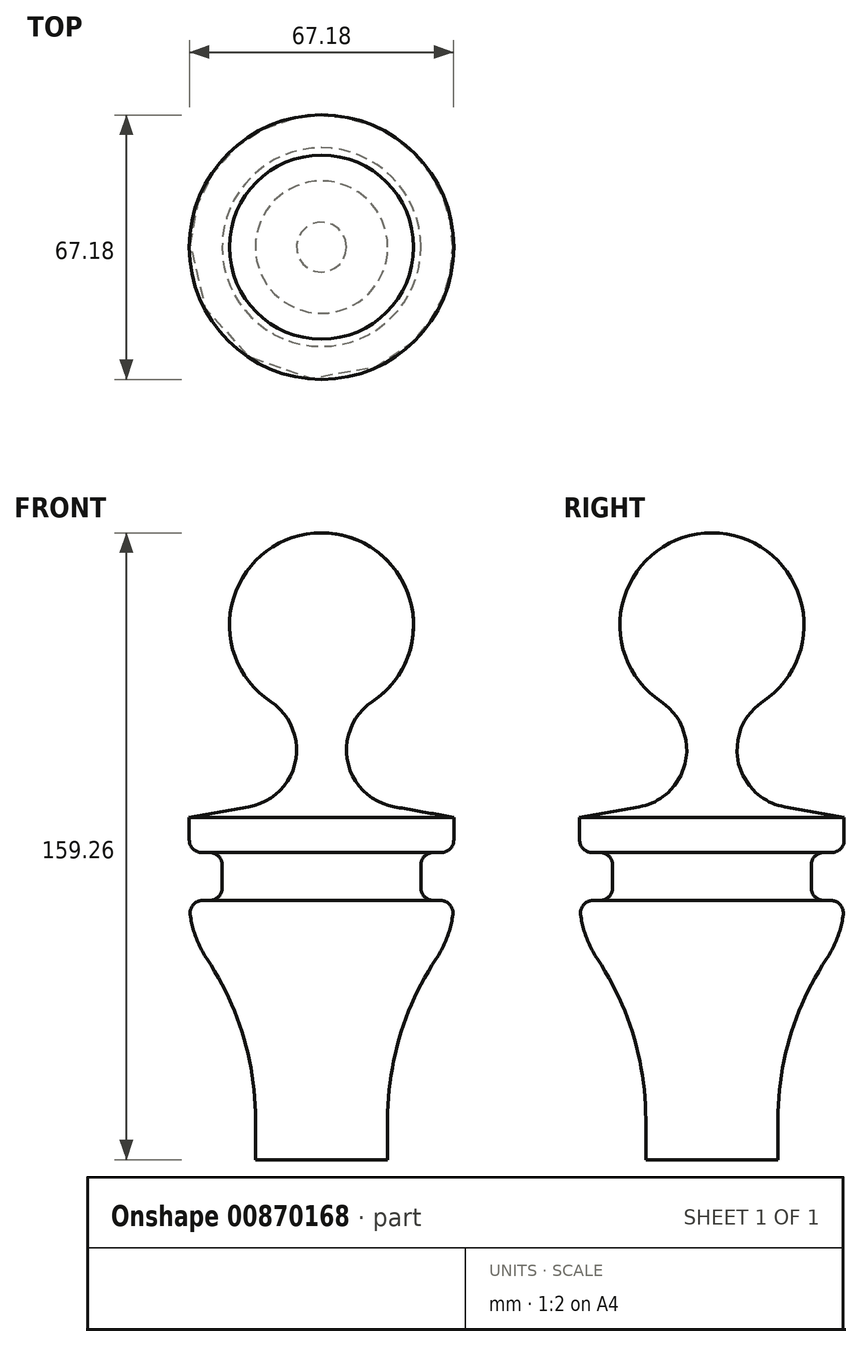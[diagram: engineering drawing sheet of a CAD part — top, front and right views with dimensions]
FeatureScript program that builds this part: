
annotation { "Feature Type Name" : "Feature", "Feature Type Description" : "" }
export const myFeature = defineFeature(function(context is Context, id is Id, definition is map)
    precondition{}
    {
        {
            var Q0;
            Q0=qCreatedBy(makeId("Front.planeOp"),FACE);
            var sketch = newSketch(context, id + "F0", { "sketchPlane" : qUnion([Q0])});
            skLineSegment(sketch, "E0", {"start": v(0, 0) * mm, "end": v(0, 159.26) * mm});
            skArc(sketch, "E1", {"start": v(0, 159.26) * mm, "mid": v(22.4, 142.62) * mm, "end": v(12.93, 116.37) * mm});
            skArc(sketch, "E2", {"start": v(12.93, 116.37) * mm, "mid": v(6.66, 101.12) * mm, "end": v(18.5, 89.65) * mm});
            skLineSegment(sketch, "E3", {"start": v(18.5, 89.65) * mm, "end": v(33.6, 86.98) * mm});
            skLineSegment(sketch, "E4", {"start": v(33.6, 86.98) * mm, "end": v(33.6, 81.21) * mm});
            skLineSegment(sketch, "E5", {"start": v(30.42, 78.04) * mm, "end": v(28.4, 78.04) * mm});
            skLineSegment(sketch, "E6", {"start": v(25.23, 74.86) * mm, "end": v(25.23, 69.04) * mm});
            skLineSegment(sketch, "E7", {"start": v(28.4, 65.86) * mm, "end": v(30.2, 65.86) * mm});
            skArc(sketch, "E8", {"start": v(29.13, 51.06) * mm, "mid": v(31.87, 56.42) * mm, "end": v(33.35, 62.26) * mm});
            skLineSegment(sketch, "E9", {"start": v(16.8, 10.18) * mm, "end": v(16.8, 0) * mm});
            skLineSegment(sketch, "E10", {"start": v(16.8, 0) * mm, "end": v(0, 0) * mm});
            skPoint(sketch, "E11.visualSharp", {"position": v(33.6, 78.04) * mm});
            skArc(sketch, "E11.filletArc", {"start": v(30.42, 78.04) * mm, "mid": v(32.66, 78.97) * mm, "end": v(33.6, 81.21) * mm});
            skPoint(sketch, "E12.visualSharp", {"position": v(33.6, 65.86) * mm});
            skArc(sketch, "E12.filletArc", {"start": v(33.35, 62.26) * mm, "mid": v(32.6, 64.78) * mm, "end": v(30.2, 65.86) * mm});
            skPoint(sketch, "E13.visualSharp", {"position": v(25.23, 78.04) * mm});
            skArc(sketch, "E13.filletArc", {"start": v(28.4, 78.04) * mm, "mid": v(26.16, 77.1) * mm, "end": v(25.23, 74.86) * mm});
            skPoint(sketch, "E14.visualSharp", {"position": v(25.23, 65.86) * mm});
            skArc(sketch, "E14.filletArc", {"start": v(25.23, 69.04) * mm, "mid": v(26.16, 66.8) * mm, "end": v(28.4, 65.86) * mm});
            skPoint(sketch, "E15.visualSharp", {"position": v(16.8, 41.02) * mm});
            skArc(sketch, "E15.filletArc", {"start": v(29.13, 51.06) * mm, "mid": v(19.95, 31.53) * mm, "end": v(16.8, 10.18) * mm});
            skLineSegment(sketch, "E16", {"start": v(0, 0) * mm, "end": v(0, -27.17) * mm, "construction": true});
            skSolve(sketch);
        }
        {
            var Q0;
            Q0 = qSketchRegion(id + "F0", true);
            var Q1;
            Q1=sQuery(id+"F0.wireOp",EDGE,"E16");
            revolve(context, id + "F1", {"surfaceOperationType" : NewSurfaceOperationType.NEW, "entities" : qUnion([Q0]), "axis" : qUnion([Q1]), "revolveType" : RevolveType.FULL});
        }
    });
